# Revit family: Grundplatten Typ II
name_source: partatom
category: HLS-Bauteile
revit_build: Autodesk Revit 2017 (Build: 20190507_1515(x64)
units: mm (PartAtom-declared; Revit-internal decimal feet)

## family parameters
Arbeitsebenenbasiert = Ja
Beim Laden mit Abzugskörper schneiden = Nein
Bemaßung runder Anschluss = Durchmesser verwenden
Gemeinsam genutzt = Ja
Immer vertikal = Nein
Raumberechnungspunkt = Nein
Teiletyp = Normal

## types (7) — shared parameters
Abmessung = 110 x 73 x 4 mm
Anzahl Befestigungsloch = 4
B = 73 mm  [stored 0.239501 ft]
B1 = 40 mm  [stored 0.131234 ft]
Breite = 73 mm  [stored 0.239501 ft]
D = 11 mm  [stored 0.0360892 ft]
Fabrikat = MEFA
Firma = MEFA Befestigungs- und Montagesysteme GmbH
Kurztext1 = Grundplatte Typ II
L = 110 mm  [stored 0.360892 ft]
L1 = 77 mm  [stored 0.252625 ft]
Lochabstand längs = 77 mm  [stored 0.252625 ft]
Lochdurchmesser = 11 mm
Länge = 110 mm  [stored 0.360892 ft]
MD = 4 mm  [stored 0.0131234 ft]
Material = Stahl
Materialname = S235
Mengeneinheit = St
Oberflaeche = galvanisch verzinkt
Stärke = 4 mm  [stored 0.0131234 ft]
Vorgabe-Ansicht = 1219 mm
max. zul. Last hängend = 3.40 kN
vpe = 50 St
zero-valued in all types: Sicherheitsfaktor

## per-type parameters (varying)
| type | Anschluss | Artikelnummer | EAN | Gewicht | Gewicht pro Bauteil | Gewindeanschluss | H | HGA | Kurztext2 |
| Grundplatte Typ II 110x73x4,0  M 8 | M8 | 059050701 | 4250928457837 | 0.26 kg | 0.26 kg | 6kt-Mutter parametrik : Hutmutter gedreht M8 (4130008) | 16 mm  [stored 0.0524934 ft] | 12 mm  [stored 0.0393701 ft] | Anschluss M8 Platte 110x73x4 mm |
| Grundplatte Typ II 110x73x4,0  M10 | M10 | 059054101 | 4250928457844 | 0.27 kg | 0.27 kg | 6kt-Mutter parametrik : Hutmutter gedreht M10 (4130010) | 18 mm  [stored 0.0590551 ft] | 14 mm  [stored 0.0459318 ft] | Anschluss M10 Platte 110x73x4 mm |
| Grundplatte Typ II 110x73x4,0  M12 | M12 | 059052501 | 4250928457851 | 0.27 kg | 0.27 kg | 6kt-Mutter parametrik : Hutmutter gedreht M12 (4130012) | 20 mm  [stored 0.0656168 ft] | 16 mm  [stored 0.0524934 ft] | Anschluss M12 Platte 110x73x4 mm |
| Grundplatte Typ II 110x73x4,0  M16 | M16 | 059053301 | 4250928457868 | 0.30 kg | 0.30 kg | 6kt-Mutter parametrik : Hutmutter M16 (4130016) | 24 mm  [stored 0.0787402 ft] | 20 mm  [stored 0.0656168 ft] | Anschluss M16 Platte 110x73x4 mm |
| Grundplatte Typ II 110x73x4,0  1/2" | 1/2'' | 059050901 | 4250928415165 | 0.28 kg | 0.28 kg | Runde Gewindeanschlusse parametrik : A4 Schweißmuffe 1/2´´ | 19 mm  [stored 0.062336 ft] | 15 mm  [stored 0.0492126 ft] | Anschluss 1/2'' Platte 110x73x4 mm |
| Grundplatte Typ II 110x73x4,0  3/4" | 3/4'' | 059051701 | 4250928457875 | 0.29 kg | 0.29 kg | Runde Gewindeanschlusse parametrik : Schweißmuffe 3/4´´ (0009873) | 21 mm  [stored 0.0688976 ft] | 17 mm | Anschluss 3/4'' Platte 110x73x4 mm |
| Grundplatte Typ II 110x73x4,0  1" | 1'' | 059056801 | 4250928457882 | 0.32 kg | 0.32 kg | Runde Gewindeanschlusse parametrik : A4 Schweißmuffe 1´´ (0009870) | 24 mm  [stored 0.0787402 ft] | 20 mm  [stored 0.0656168 ft] | Anschluss 1'' Platte 110x73x4 mm |

note: [stored X ft] marks values corroborated as IEEE doubles in the binary element streams (Revit-internal decimal feet)

## geometry (parser evidence)
native form markers: Sweep x3
no freeform markers — native parametric forms only
